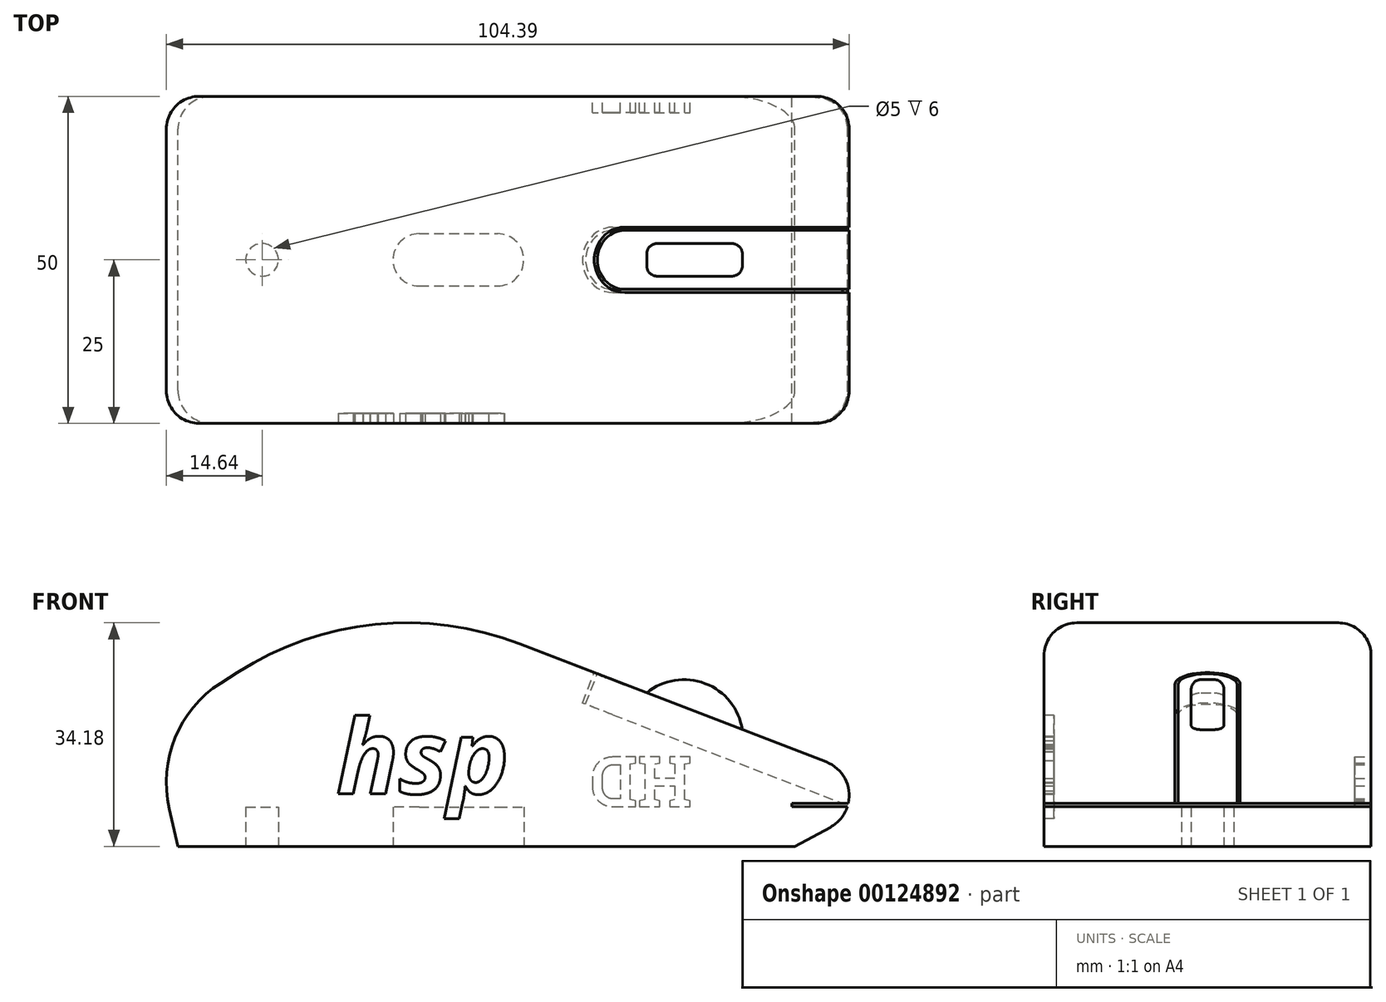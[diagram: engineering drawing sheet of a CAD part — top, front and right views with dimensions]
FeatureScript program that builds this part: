
annotation { "Feature Type Name" : "Feature", "Feature Type Description" : "" }
export const myFeature = defineFeature(function(context is Context, id is Id, definition is map)
    precondition{}
    {
        {
            var Q0;
            Q0=qCreatedBy(makeId("Front.planeOp"),FACE);
            var sketch = newSketch(context, id + "F0", { "sketchPlane" : qUnion([Q0])});
            skLineSegment(sketch, "E0", {"start": v(-42.86, 0) * mm, "end": v(51.43, 0) * mm});
            skLineSegment(sketch, "E1", {"start": v(-42.86, 0) * mm, "end": v(-47.02, 18.12) * mm});
            skLineSegment(sketch, "E2", {"start": v(67.38, 8.6) * mm, "end": v(-13.32, 39.71) * mm});
            skLineSegment(sketch, "E3", {"start": v(-13.32, 39.71) * mm, "end": v(-47.02, 18.12) * mm});
            skPoint(sketch, "E4.endSnap0", {"position": v(51.43, 8.6) * mm});
            skLineSegment(sketch, "E5", {"start": v(51.43, 0) * mm, "end": v(67.38, 8.6) * mm});
            skSolve(sketch);
        }
        {
            var Q0;
            Q0 = qSketchRegion(id + "F0", true);
            var Q1;
            Q1=makeQuery(id+"F0.imprint","IMPRINT",FACE,{"disambiguationData":[TD([[makeQuery(id+"F0.imprint","IMPRINT",EDGE,{"derivedFrom":sQuery(id+"F0.wireOp",EDGE,"E0")}),1.0]])]});
            extrude(context, id + "F1", {"entities" : qUnion([Q0, Q1]), "depth" : 50 * mm, "symmetric" : true});
        }
        {
            var Q0;
            Q0=makeQuery(id+"F1.opExtrude","SWEPT_EDGE",EDGE,{"disambiguationData":[OSD([sQuery(id+"F0.wireOp",EDGE,"E2"),sQuery(id+"F0.wireOp",EDGE,"E5")])]});
            fillet(context, id + "F2", {"entities" : qUnion([Q0]), "radius" : 5.5 * mm, "tangentPropagation" : true, "allowEdgeOverflow" : false});
        }
        {
            var Q0;
            Q0=makeQuery(id+"F1.opExtrude","SWEPT_EDGE",EDGE,{"disambiguationData":[OSD([sQuery(id+"F0.wireOp",EDGE,"E2"),sQuery(id+"F0.wireOp",EDGE,"E3")])]});
            fillet(context, id + "F3", {"entities" : qUnion([Q0]), "radius" : 48 * mm, "tangentPropagation" : true, "allowEdgeOverflow" : false});
        }
        {
            var Q0;
            Q0=makeQuery(id+"F1.opExtrude","SWEPT_EDGE",EDGE,{"disambiguationData":[OSD([sQuery(id+"F0.wireOp",EDGE,"E1"),sQuery(id+"F0.wireOp",EDGE,"E3")])]});
            fillet(context, id + "F4", {"entities" : qUnion([Q0]), "radius" : 18 * mm, "tangentPropagation" : true, "allowEdgeOverflow" : false});
        }
        {
            var Q0;
            Q0=makeQuery(id+"F1.opExtrude","CAP_EDGE",EDGE,{"disambiguationData":[OSD([sQuery(id+"F0.wireOp",EDGE,"E2")])],"isStart":false});
            var Q1;
            Q1=makeQuery(id+"F1.opExtrude","CAP_EDGE",EDGE,{"disambiguationData":[OSD([sQuery(id+"F0.wireOp",EDGE,"E2")])],"isStart":true});
            fillet(context, id + "F5", {"entities" : qUnion([Q0, Q1]), "radius" : 5 * mm, "tangentPropagation" : true, "allowEdgeOverflow" : false});
        }
        {
            var Q0;
            Q0=qCreatedBy(makeId("Front.planeOp"),FACE);
            var sketch = newSketch(context, id + "F6", { "sketchPlane" : qUnion([Q0])});
            skCircle(sketch, "E6", {"center": v(34.5, 16.5) * mm, "radius": 9 * mm});
            skSolve(sketch);
        }
        {
            var Q0;
            Q0=makeQuery(id+"F6.imprint","IMPRINT",FACE,{"disambiguationData":[TD([[makeQuery(id+"F6.imprint","IMPRINT",EDGE,{"derivedFrom":sQuery(id+"F6.wireOp",EDGE,"E6")}),1.0]])]});
            extrude(context, id + "F7", {"entities" : qUnion([Q0]), "operationType" : NewBodyOperationType.ADD, "depth" : 5 * mm, "symmetric" : true});
        }
        {
            var Q0;
            Q0=makeQuery(id+"F7.opExtrude","CAP_EDGE",EDGE,{"disambiguationData":[OSD([sQuery(id+"F6.wireOp",EDGE,"E6")])],"isStart":true});
            var Q1;
            Q1=makeQuery(id+"F7.opExtrude","CAP_EDGE",EDGE,{"disambiguationData":[OSD([sQuery(id+"F6.wireOp",EDGE,"E6")])],"isStart":false});
            fillet(context, id + "F8", {"entities" : qUnion([Q0, Q1]), "radius" : 1.5 * mm, "tangentPropagation" : true, "allowEdgeOverflow" : false});
        }
        {
            var Q0;
            Q0=makeQuery(id+"F1.opExtrude","SWEPT_FACE",FACE,{"disambiguationData":[OSD([sQuery(id+"F0.wireOp",EDGE,"E2")])]});
            var sketch = newSketch(context, id + "F9", { "sketchPlane" : qUnion([Q0])});
            skLineSegment(sketch, "E7.bottom", {"start": v(14.82, 5) * mm, "end": v(58.27, 5) * mm});
            skLineSegment(sketch, "E7.top", {"start": v(14.82, -5) * mm, "end": v(58.27, -5) * mm});
            skArc(sketch, "E8", {"start": v(14.82, 5) * mm, "mid": v(9.82, 0) * mm, "end": v(14.82, -5) * mm});
            skLineSegment(sketch, "E9.0", {"start": v(14.82, 4.5) * mm, "end": v(58.27, 4.5) * mm});
            skLineSegment(sketch, "E10.0", {"start": v(14.82, -4.5) * mm, "end": v(58.27, -4.5) * mm});
            skArc(sketch, "E11.0", {"start": v(14.82, 4.5) * mm, "mid": v(10.32, 0) * mm, "end": v(14.82, -4.5) * mm});
            skLineSegment(sketch, "E12", {"start": v(58.27, 4.5) * mm, "end": v(58.27, 5) * mm});
            skPoint(sketch, "E13.orphan", {"position": v(58.27, -5) * mm});
            skPoint(sketch, "E14.orphan", {"position": v(47.82, -5) * mm});
            skLineSegment(sketch, "E15", {"start": v(58.27, -5) * mm, "end": v(58.27, -4.5) * mm});
            skSolve(sketch);
        }
        {
            var Q0;
            Q0 = qSketchRegion(id + "F9", true);
            var Q1;
            {var subQ3=sQuery(id+"F9.wireOp",EDGE,"E7.bottom");Q1=makeQuery(id+"F9.imprint","IMPRINT",FACE,{"disambiguationData":[TD([[makeQuery(id+"F9.imprint","IMPRINT",EDGE,{"derivedFrom":subQ3}),-1.0]])]});}
            extrude(context, id + "F10", {"entities" : qUnion([Q0, Q1]), "operationType" : NewBodyOperationType.REMOVE, "oppositeDirection" : true, "depth" : 5 * mm});
        }
        {
            var Q0;
            Q0=makeQuery(id+"F1.opExtrude","SWEPT_FACE",FACE,{"disambiguationData":[OSD([sQuery(id+"F0.wireOp",EDGE,"E0")])]});
            var sketch = newSketch(context, id + "F11", { "sketchPlane" : qUnion([Q0])});
            skCircle(sketch, "E16", {"center": v(-30, 0) * mm, "radius": 2.5 * mm});
            skLineSegment(sketch, "E17.bottom", {"start": v(-6, 4) * mm, "end": v(6, 4) * mm});
            skLineSegment(sketch, "E17.top", {"start": v(-6, -4) * mm, "end": v(6, -4) * mm});
            skArc(sketch, "E18", {"start": v(-6, 4) * mm, "mid": v(-10, 0) * mm, "end": v(-6, -4) * mm});
            skArc(sketch, "E19.MirrorCS", {"start": v(6, 4) * mm, "mid": v(10, 0) * mm, "end": v(6, -4) * mm});
            skSolve(sketch);
        }
        {
            var Q0;
            Q0=makeQuery(id+"F11.imprint","IMPRINT",FACE,{"disambiguationData":[TD([[makeQuery(id+"F11.imprint","IMPRINT",EDGE,{"derivedFrom":sQuery(id+"F11.wireOp",EDGE,"E17.bottom")}),-1.0]])]});
            var Q1;
            Q1=makeQuery(id+"F11.imprint","IMPRINT",FACE,{"disambiguationData":[TD([[makeQuery(id+"F11.imprint","IMPRINT",EDGE,{"derivedFrom":sQuery(id+"F11.wireOp",EDGE,"E16")}),1.0]])]});
            extrude(context, id + "F12", {"entities" : qUnion([Q0, Q1]), "operationType" : NewBodyOperationType.REMOVE, "oppositeDirection" : true, "depth" : 6 * mm});
        }
        {
            var Q0;
            Q0=qCreatedBy(makeId("Right.planeOp"),FACE);
            cPlane(context, id + "F13", {"entities" : qUnion([Q0]), "cplaneType" : CPlaneType.OFFSET, "offset" : 56 * mm, "width" : 150 * mm, "height" : 150 * mm});
        }
        {
            var Q0;
            Q0=qCreatedBy(id+"F13.planeOp",FACE);
            var sketch = newSketch(context, id + "F14", { "sketchPlane" : qUnion([Q0])});
            skLineSegment(sketch, "E20", {"start": v(-27.35, 6.07) * mm, "end": v(27.35, 6.07) * mm});
            skLineSegment(sketch, "E21.0", {"start": v(-27.35, 6.57) * mm, "end": v(27.35, 6.57) * mm});
            skLineSegment(sketch, "E22", {"start": v(-27.35, 6.57) * mm, "end": v(-27.35, 6.07) * mm});
            skLineSegment(sketch, "E23.MirrorCS", {"start": v(27.35, 6.57) * mm, "end": v(27.35, 6.07) * mm});
            skPoint(sketch, "E24.start.orphan", {"position": v(0, 6.57) * mm});
            skSolve(sketch);
        }
        {
            var Q0;
            Q0=makeQuery(id+"F14.imprint","IMPRINT",FACE,{"disambiguationData":[TD([[makeQuery(id+"F14.imprint","IMPRINT",EDGE,{"derivedFrom":sQuery(id+"F14.wireOp",EDGE,"E20")}),1.0]])]});
            extrude(context, id + "F15", {"entities" : qUnion([Q0]), "operationType" : NewBodyOperationType.REMOVE, "oppositeDirection" : true, "depth" : (10) * mm, "symmetric" : true});
        }
        {
            var Q0;
            Q0=makeQuery(id+"F1.opExtrude","CAP_FACE",FACE,{"disambiguationData":[OSD([sQuery(id+"F0.wireOp",EDGE,"E0"),sQuery(id+"F0.wireOp",EDGE,"E1"),sQuery(id+"F0.wireOp",EDGE,"E2"),sQuery(id+"F0.wireOp",EDGE,"E3"),sQuery(id+"F0.wireOp",EDGE,"E5")])],"isStart":false});
            var sketch = newSketch(context, id + "F16", { "sketchPlane" : qUnion([Q0])});
            skText(sketch, "E25", { "text": "hsp ", "fontName": "OpenSans-BoldItalic.ttf"});
            const initialGuessF16  = {"E25": [-0.01866, 0.00805, 1, 0, 0.01137]};
            skSetInitialGuess(sketch, initialGuessF16);
            skSolve(sketch);
        }
        {
            var Q0;
            Q0 = qSketchRegion(id + "F16", true);
            extrude(context, id + "F17", {"entities" : qUnion([Q0]), "operationType" : NewBodyOperationType.REMOVE, "oppositeDirection" : true, "depth" : 1.5 * mm});
        }
        {
            var Q0;
            Q0=makeQuery(id+"F1.opExtrude","CAP_FACE",FACE,{"disambiguationData":[OSD([sQuery(id+"F0.wireOp",EDGE,"E0"),sQuery(id+"F0.wireOp",EDGE,"E1"),sQuery(id+"F0.wireOp",EDGE,"E2"),sQuery(id+"F0.wireOp",EDGE,"E3"),sQuery(id+"F0.wireOp",EDGE,"E5")])],"isStart":true});
            var sketch = newSketch(context, id + "F18", { "sketchPlane" : qUnion([Q0])});
            skText(sketch, "E26", { "text": "HD", "fontName": "RobotoSlab-Bold.ttf"});
            const initialGuessF18  = {"E26": [-0.03572, 0.00608, 1, 0, 0.00768]};
            skSetInitialGuess(sketch, initialGuessF18);
            skSolve(sketch);
        }
        {
            var Q0;
            Q0 = qSketchRegion(id + "F18", true);
            extrude(context, id + "F19", {"entities" : qUnion([Q0]), "operationType" : NewBodyOperationType.REMOVE, "oppositeDirection" : true, "depth" : 2.5 * mm, "offsetDistance" : 25 * mm});
        }
    });
